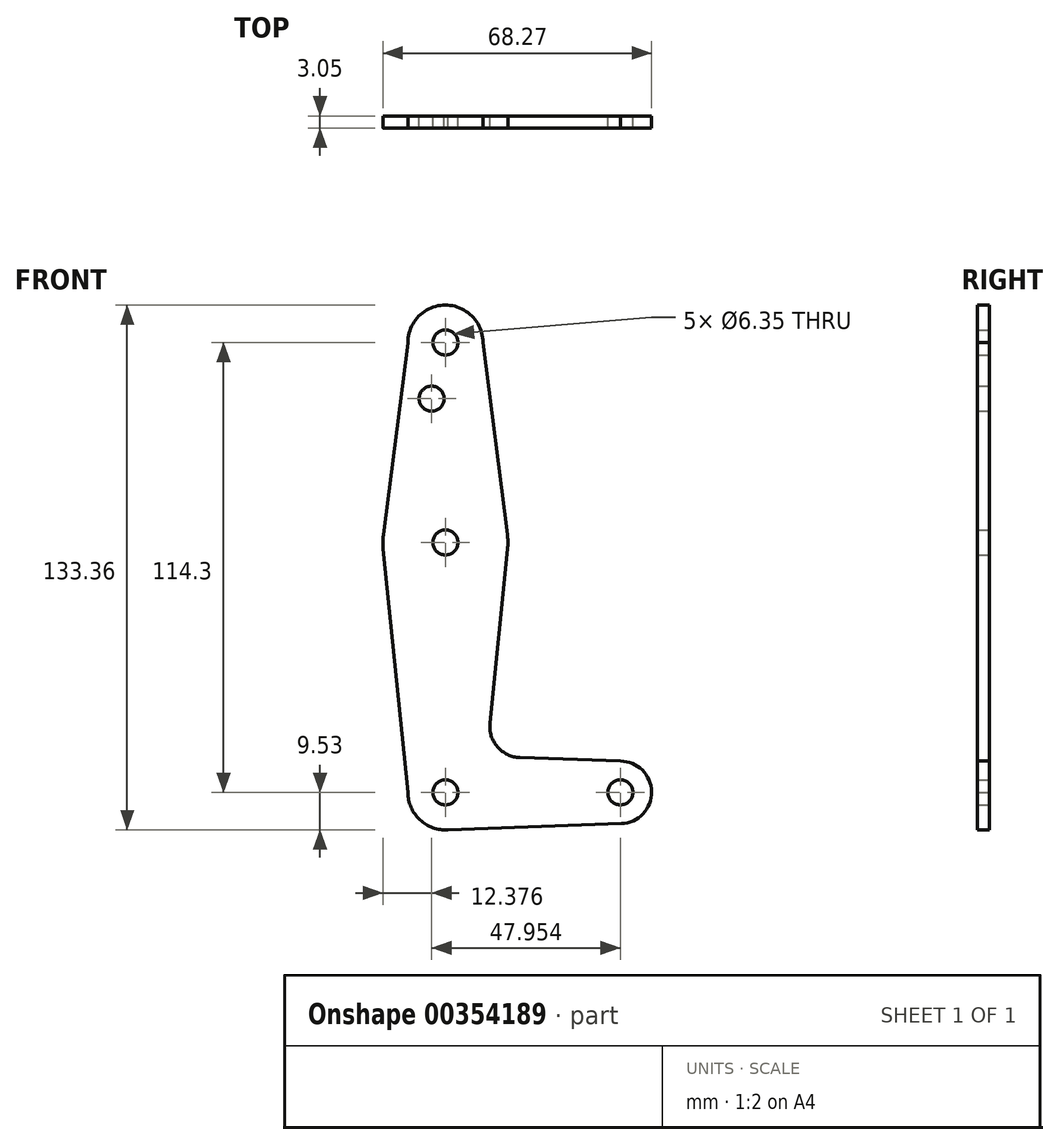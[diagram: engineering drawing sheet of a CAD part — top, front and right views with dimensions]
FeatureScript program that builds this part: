
annotation { "Feature Type Name" : "Feature", "Feature Type Description" : "" }
export const myFeature = defineFeature(function(context is Context, id is Id, definition is map)
    precondition{}
    {
        {
            var Q0;
            Q0=qCreatedBy(makeId("Front.planeOp"),FACE);
            var sketch = newSketch(context, id + "F0", { "sketchPlane" : qUnion([Q0])});
            skLineSegment(sketch, "E0", {"start": v(0, 0) * mm, "end": v(44.45, 0) * mm});
            skLineSegment(sketch, "E1", {"start": v(0, 0) * mm, "end": v(0, 63.5) * mm});
            skLineSegment(sketch, "E2", {"start": v(0, 63.5) * mm, "end": v(0, 114.3) * mm});
            skCircle(sketch, "E3", {"center": v(44.45, 0) * mm, "radius": 7.94 * mm});
            skCircle(sketch, "E4", {"center": v(0, 0) * mm, "radius": 9.53 * mm});
            skCircle(sketch, "E5", {"center": v(0, 63.5) * mm, "radius": 15.88 * mm});
            skCircle(sketch, "E6", {"center": v(0, 114.3) * mm, "radius": 9.53 * mm});
            skLineSegment(sketch, "E7", {"start": v(-9.52, 114.21) * mm, "end": v(-15.75, 65.51) * mm});
            skLineSegment(sketch, "E8", {"start": v(-9.53, 0) * mm, "end": v(-15.8, 61.9) * mm});
            skLineSegment(sketch, "E9", {"start": v(9.53, 114.3) * mm, "end": v(15.75, 65.5) * mm});
            skLineSegment(sketch, "E10", {"start": v(11.3, 17.6) * mm, "end": v(15.8, 61.9) * mm});
            skLineSegment(sketch, "E11", {"start": v(18.93, 8.85) * mm, "end": v(44.45, 7.94) * mm});
            skCircle(sketch, "E12", {"center": v(0, 114.3) * mm, "radius": 3.18 * mm});
            skCircle(sketch, "E13", {"center": v(0, 63.5) * mm, "radius": 3.18 * mm});
            skCircle(sketch, "E14", {"center": v(44.45, 0) * mm, "radius": 3.18 * mm});
            skCircle(sketch, "E15", {"center": v(0, 0) * mm, "radius": 3.18 * mm});
            skCircle(sketch, "E16", {"center": v(-3.5, 100.03) * mm, "radius": 3.18 * mm});
            skArc(sketch, "E17.filletArc", {"start": v(11.3, 17.6) * mm, "mid": v(13.22, 11.57) * mm, "end": v(18.93, 8.85) * mm});
            skLineSegment(sketch, "E18", {"start": v(0, -9.53) * mm, "end": v(44.73, -7.93) * mm});
            skSolve(sketch);
        }
        {
            var Q0;
            Q0 = qSketchRegion(id + "F0", true);
            var Q1;
            {var subQ0=sQuery(id+"F0.wireOp",EDGE,"E15");var subQ1=sQuery(id+"F0.wireOp",EDGE,"E0");var subQ2=makeQuery(id+"F0.imprint","INTERSECT",VERTEX,{"derivedFrom":[subQ1,subQ0]});Q1=makeQuery(id+"F0.imprint","IMPRINT",FACE,{"disambiguationData":[TD([[makeQuery(id+"F0.imprint","IMPRINT",EDGE,{"disambiguationData":[TD([[subQ2,-1.0]])],"derivedFrom":subQ1}),1.0]])]});}
            extrude(context, id + "F1", {"entities" : qUnion([Q0, Q1]), "depth" : 3.05 * mm});
        }
    });
